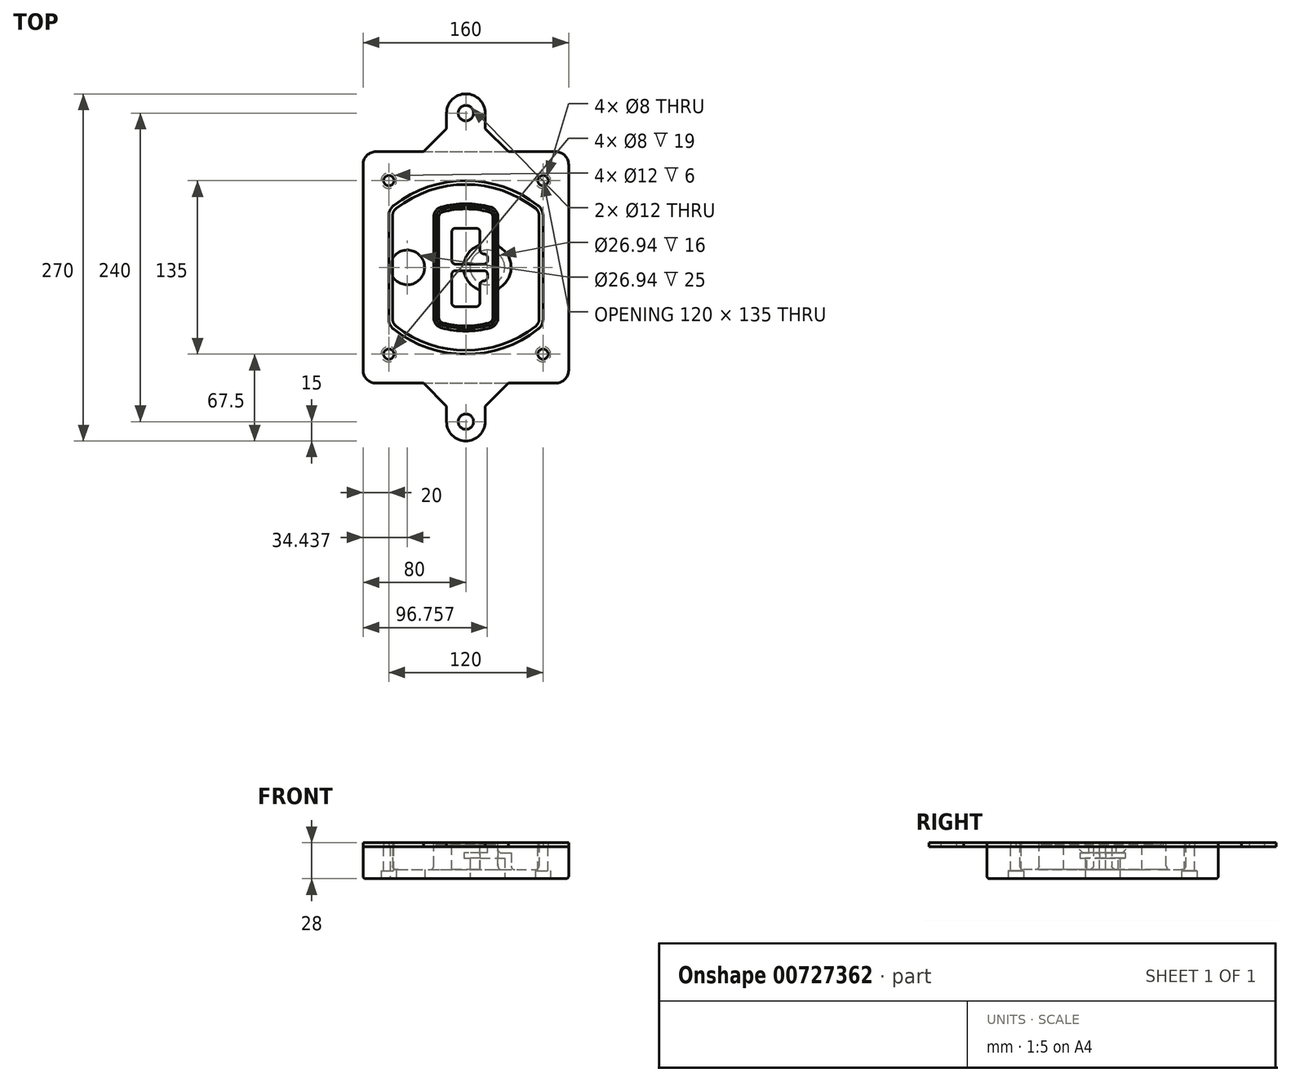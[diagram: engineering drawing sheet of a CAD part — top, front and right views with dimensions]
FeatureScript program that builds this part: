
annotation { "Feature Type Name" : "Feature", "Feature Type Description" : "" }
export const myFeature = defineFeature(function(context is Context, id is Id, definition is map)
    precondition{}
    {
        {
            var Q0;
            Q0=qCreatedBy(makeId("Top.planeOp"),FACE);
            var sketch = newSketch(context, id + "F0", { "sketchPlane" : qUnion([Q0])});
            skPoint(sketch, "E0.rect.middle", {"position": v(0, 0) * mm});
            skLineSegment(sketch, "E1.bottom", {"start": v(-70, -90) * mm, "end": v(70, -90) * mm});
            skLineSegment(sketch, "E1.top", {"start": v(-70, 90) * mm, "end": v(70, 90) * mm});
            skLineSegment(sketch, "E1.left", {"start": v(-80, -80) * mm, "end": v(-80, 80) * mm});
            skLineSegment(sketch, "E1.right", {"start": v(80, -80) * mm, "end": v(80, 80) * mm});
            skLineSegment(sketch, "E2", {"start": v(-80, 90) * mm, "end": v(80, -90) * mm, "construction": true});
            skLineSegment(sketch, "E3", {"start": v(80, 90) * mm, "end": v(-80, -90) * mm, "construction": true});
            skCircle(sketch, "E4", {"center": v(-60, 67.5) * mm, "radius": 4 * mm});
            skCircle(sketch, "E5", {"center": v(60, 67.5) * mm, "radius": 4 * mm});
            skCircle(sketch, "E6", {"center": v(60, -67.5) * mm, "radius": 4 * mm});
            skCircle(sketch, "E7", {"center": v(-60, -67.5) * mm, "radius": 4 * mm});
            skLineSegment(sketch, "E8", {"start": v(-60, 67.5) * mm, "end": v(60, 67.5) * mm, "construction": true});
            skLineSegment(sketch, "E9", {"start": v(60, 67.5) * mm, "end": v(60, -67.5) * mm, "construction": true});
            skLineSegment(sketch, "E10", {"start": v(60, -67.5) * mm, "end": v(-60, -67.5) * mm, "construction": true});
            skLineSegment(sketch, "E11", {"start": v(-60, -67.5) * mm, "end": v(-60, 67.5) * mm, "construction": true});
            skLineSegment(sketch, "E12", {"start": v(-60, 40.3) * mm, "end": v(-60, -40.3) * mm});
            skLineSegment(sketch, "E13", {"start": v(60, 40.3) * mm, "end": v(60, -40.3) * mm});
            skArc(sketch, "E14", {"start": v(56.15, 48.18) * mm, "mid": v(0, 67.5) * mm, "end": v(-56.15, 48.18) * mm});
            skArc(sketch, "E15", {"start": v(-56.15, -48.18) * mm, "mid": v(0, -67.5) * mm, "end": v(56.15, -48.18) * mm});
            skLineSegment(sketch, "E16", {"start": v(-60, 0) * mm, "end": v(60, 0) * mm, "construction": true});
            skPoint(sketch, "E17.visualSharp", {"position": v(-60, -45) * mm});
            skArc(sketch, "E17.filletArc", {"start": v(-60, -40.3) * mm, "mid": v(-58.99, -44.68) * mm, "end": v(-56.15, -48.18) * mm});
            skPoint(sketch, "E18.visualSharp", {"position": v(-60, 45) * mm});
            skArc(sketch, "E18.filletArc", {"start": v(-56.15, 48.18) * mm, "mid": v(-58.99, 44.68) * mm, "end": v(-60, 40.3) * mm});
            skPoint(sketch, "E19.visualSharp", {"position": v(60, 45) * mm});
            skArc(sketch, "E19.filletArc", {"start": v(60, 40.3) * mm, "mid": v(58.99, 44.68) * mm, "end": v(56.15, 48.18) * mm});
            skPoint(sketch, "E20.visualSharp", {"position": v(60, -45) * mm});
            skArc(sketch, "E20.filletArc", {"start": v(56.15, -48.18) * mm, "mid": v(58.99, -44.68) * mm, "end": v(60, -40.3) * mm});
            skPoint(sketch, "E21.visualSharp", {"position": v(-80, 90) * mm});
            skArc(sketch, "E21.filletArc", {"start": v(-70, 90) * mm, "mid": v(-77.07, 87.07) * mm, "end": v(-80, 80) * mm});
            skPoint(sketch, "E22.visualSharp", {"position": v(80, 90) * mm});
            skArc(sketch, "E22.filletArc", {"start": v(80, 80) * mm, "mid": v(77.07, 87.07) * mm, "end": v(70, 90) * mm});
            skPoint(sketch, "E23.visualSharp", {"position": v(80, -90) * mm});
            skArc(sketch, "E23.filletArc", {"start": v(70, -90) * mm, "mid": v(77.07, -87.07) * mm, "end": v(80, -80) * mm});
            skPoint(sketch, "E24.visualSharp", {"position": v(-80, -90) * mm});
            skArc(sketch, "E24.filletArc", {"start": v(-80, -80) * mm, "mid": v(-77.07, -87.07) * mm, "end": v(-70, -90) * mm});
            skArc(sketch, "E25.0", {"start": v(57, 40.3) * mm, "mid": v(56.3, 43.36) * mm, "end": v(54.3, 45.81) * mm});
            skLineSegment(sketch, "E25.1", {"start": v(57, 40.3) * mm, "end": v(57, -40.3) * mm});
            skArc(sketch, "E25.2", {"start": v(54.3, -45.81) * mm, "mid": v(56.3, -43.36) * mm, "end": v(57, -40.3) * mm});
            skArc(sketch, "E25.3", {"start": v(-54.3, -45.81) * mm, "mid": v(0, -64.5) * mm, "end": v(54.3, -45.81) * mm});
            skArc(sketch, "E25.4", {"start": v(-57, -40.3) * mm, "mid": v(-56.3, -43.36) * mm, "end": v(-54.3, -45.81) * mm});
            skArc(sketch, "E25.5", {"start": v(54.3, 45.81) * mm, "mid": v(0, 64.5) * mm, "end": v(-54.3, 45.81) * mm});
            skLineSegment(sketch, "E25.6", {"start": v(-57, 40.3) * mm, "end": v(-57, -40.3) * mm});
            skArc(sketch, "E25.7", {"start": v(-54.3, 45.81) * mm, "mid": v(-56.3, 43.36) * mm, "end": v(-57, 40.3) * mm});
            skArc(sketch, "E26.0", {"start": v(-58.62, 51.33) * mm, "mid": v(-62.58, 46.43) * mm, "end": v(-64, 40.3) * mm});
            skArc(sketch, "E26.1", {"start": v(58.62, 51.33) * mm, "mid": v(0, 71.5) * mm, "end": v(-58.62, 51.33) * mm});
            skArc(sketch, "E26.2", {"start": v(64, 40.3) * mm, "mid": v(62.58, 46.43) * mm, "end": v(58.62, 51.33) * mm});
            skLineSegment(sketch, "E26.3", {"start": v(64, 40.3) * mm, "end": v(64, -40.3) * mm});
            skArc(sketch, "E26.4", {"start": v(58.62, -51.33) * mm, "mid": v(62.58, -46.43) * mm, "end": v(64, -40.3) * mm});
            skLineSegment(sketch, "E26.5", {"start": v(-64, 40.3) * mm, "end": v(-64, -40.3) * mm});
            skArc(sketch, "E26.6", {"start": v(-58.62, -51.33) * mm, "mid": v(0, -71.5) * mm, "end": v(58.62, -51.33) * mm});
            skArc(sketch, "E26.7", {"start": v(-64, -40.3) * mm, "mid": v(-62.58, -46.43) * mm, "end": v(-58.62, -51.33) * mm});
            skSolve(sketch);
        }
        {
            var Q0;
            Q0=makeQuery(id+"F0.imprint","IMPRINT",FACE,{"disambiguationData":[TD([[makeQuery(id+"F0.imprint","IMPRINT",EDGE,{"derivedFrom":sQuery(id+"F0.wireOp",EDGE,"E1.bottom")}),1.0]])]});
            var Q1;
            Q1=makeQuery(id+"F0.imprint","IMPRINT",FACE,{"disambiguationData":[TD([[makeQuery(id+"F0.imprint","IMPRINT",EDGE,{"derivedFrom":sQuery(id+"F0.wireOp",EDGE,"E12")}),1.0]])]});
            var Q2;
            Q2=makeQuery(id+"F0.imprint","IMPRINT",FACE,{"disambiguationData":[TD([[makeQuery(id+"F0.imprint","IMPRINT",EDGE,{"derivedFrom":sQuery(id+"F0.wireOp",EDGE,"E25.0")}),1.0]])]});
            var Q3;
            Q3=makeQuery(id+"F0.imprint","IMPRINT",FACE,{"disambiguationData":[TD([[makeQuery(id+"F0.imprint","IMPRINT",EDGE,{"derivedFrom":sQuery(id+"F0.wireOp",EDGE,"E12")}),-1.0]])]});
            extrude(context, id + "F1", {"entities" : qUnion([Q0, Q1, Q2, Q3]), "oppositeDirection" : true, "depth" : 25 * mm});
        }
        {
            var Q0;
            Q0=makeQuery(id+"F0.imprint","IMPRINT",FACE,{"disambiguationData":[TD([[makeQuery(id+"F0.imprint","IMPRINT",EDGE,{"derivedFrom":sQuery(id+"F0.wireOp",EDGE,"E12")}),1.0]])]});
            extrude(context, id + "F2", {"entities" : qUnion([Q0]), "operationType" : NewBodyOperationType.ADD, "depth" : 3 * mm});
        }
        {
            var Q0;
            Q0=makeQuery(id+"F0.imprint","IMPRINT",FACE,{"disambiguationData":[TD([[makeQuery(id+"F0.imprint","IMPRINT",EDGE,{"derivedFrom":sQuery(id+"F0.wireOp",EDGE,"E25.0")}),1.0]])]});
            extrude(context, id + "F3", {"entities" : qUnion([Q0]), "operationType" : NewBodyOperationType.REMOVE, "oppositeDirection" : true, "depth" : 18 * mm});
        }
        {
            var Q0;
            Q0=makeQuery(id+"F2.opExtrude","CAP_FACE",FACE,{"disambiguationData":[OSD([sQuery(id+"F0.wireOp",EDGE,"E12"),sQuery(id+"F0.wireOp",EDGE,"E13"),sQuery(id+"F0.wireOp",EDGE,"E14"),sQuery(id+"F0.wireOp",EDGE,"E15"),sQuery(id+"F0.wireOp",EDGE,"E17.filletArc"),sQuery(id+"F0.wireOp",EDGE,"E18.filletArc"),sQuery(id+"F0.wireOp",EDGE,"E19.filletArc"),sQuery(id+"F0.wireOp",EDGE,"E20.filletArc"),sQuery(id+"F0.wireOp",EDGE,"E25.0"),sQuery(id+"F0.wireOp",EDGE,"E25.1"),sQuery(id+"F0.wireOp",EDGE,"E25.2"),sQuery(id+"F0.wireOp",EDGE,"E25.3"),sQuery(id+"F0.wireOp",EDGE,"E25.4"),sQuery(id+"F0.wireOp",EDGE,"E25.5"),sQuery(id+"F0.wireOp",EDGE,"E25.6"),sQuery(id+"F0.wireOp",EDGE,"E25.7")])],"isStart":false});
            var sketch = newSketch(context, id + "F4", { "sketchPlane" : qUnion([Q0])});
            skArc(sketch, "E27.0", {"start": v(-19.08, -46.97) * mm, "mid": v(0, -49.5) * mm, "end": v(19.08, -46.97) * mm});
            skArc(sketch, "E28.0", {"start": v(19.08, 46.97) * mm, "mid": v(0, 49.5) * mm, "end": v(-19.08, 46.97) * mm});
            skLineSegment(sketch, "E29", {"start": v(-25, 39.25) * mm, "end": v(-25, -39.25) * mm});
            skLineSegment(sketch, "E30", {"start": v(25, 39.25) * mm, "end": v(25, -39.25) * mm});
            skLineSegment(sketch, "E31", {"start": v(-25, 45.1) * mm, "end": v(25, 45.1) * mm, "construction": true});
            skLineSegment(sketch, "E32", {"start": v(-25, -45.1) * mm, "end": v(25, -45.1) * mm, "construction": true});
            skPoint(sketch, "E33.visualSharp", {"position": v(-25, 45.1) * mm});
            skArc(sketch, "E33.filletArc", {"start": v(-19.08, 46.97) * mm, "mid": v(-23.35, 44.11) * mm, "end": v(-25, 39.25) * mm});
            skPoint(sketch, "E34.visualSharp", {"position": v(25, 45.1) * mm});
            skArc(sketch, "E34.filletArc", {"start": v(25, 39.25) * mm, "mid": v(23.35, 44.11) * mm, "end": v(19.08, 46.97) * mm});
            skPoint(sketch, "E35.visualSharp", {"position": v(25, -45.1) * mm});
            skArc(sketch, "E35.filletArc", {"start": v(19.08, -46.97) * mm, "mid": v(23.35, -44.11) * mm, "end": v(25, -39.25) * mm});
            skPoint(sketch, "E36.visualSharp", {"position": v(-25, -45.1) * mm});
            skArc(sketch, "E36.filletArc", {"start": v(-25, -39.25) * mm, "mid": v(-23.35, -44.11) * mm, "end": v(-19.08, -46.97) * mm});
            skArc(sketch, "E37.0", {"start": v(54.3, 45.81) * mm, "mid": v(0, 64.5) * mm, "end": v(-54.3, 45.81) * mm});
            skArc(sketch, "E37.1", {"start": v(-54.3, 45.81) * mm, "mid": v(-56.3, 43.36) * mm, "end": v(-57, 40.3) * mm});
            skLineSegment(sketch, "E37.2", {"start": v(-57, 40.3) * mm, "end": v(-57, -40.3) * mm});
            skArc(sketch, "E37.3", {"start": v(-57, -40.3) * mm, "mid": v(-56.3, -43.36) * mm, "end": v(-54.3, -45.81) * mm});
            skArc(sketch, "E37.4", {"start": v(-54.3, -45.81) * mm, "mid": v(0, -64.5) * mm, "end": v(54.3, -45.81) * mm});
            skArc(sketch, "E37.5", {"start": v(54.3, -45.81) * mm, "mid": v(56.3, -43.36) * mm, "end": v(57, -40.3) * mm});
            skLineSegment(sketch, "E37.6", {"start": v(57, 40.3) * mm, "end": v(57, -40.3) * mm});
            skArc(sketch, "E37.7", {"start": v(57, 40.3) * mm, "mid": v(56.3, 43.36) * mm, "end": v(54.3, 45.81) * mm});
            skLineSegment(sketch, "E38.0", {"start": v(23, 39.25) * mm, "end": v(23, -39.25) * mm});
            skArc(sketch, "E38.1", {"start": v(18.56, -45.04) * mm, "mid": v(21.76, -42.9) * mm, "end": v(23, -39.25) * mm});
            skArc(sketch, "E38.2", {"start": v(-18.56, -45.04) * mm, "mid": v(0, -47.5) * mm, "end": v(18.56, -45.04) * mm});
            skArc(sketch, "E38.3", {"start": v(-23, -39.25) * mm, "mid": v(-21.76, -42.9) * mm, "end": v(-18.56, -45.04) * mm});
            skLineSegment(sketch, "E38.4", {"start": v(-23, 39.25) * mm, "end": v(-23, -39.25) * mm});
            skArc(sketch, "E38.5", {"start": v(23, 39.25) * mm, "mid": v(21.76, 42.9) * mm, "end": v(18.56, 45.04) * mm});
            skArc(sketch, "E38.6", {"start": v(-18.56, 45.04) * mm, "mid": v(-21.76, 42.9) * mm, "end": v(-23, 39.25) * mm});
            skArc(sketch, "E38.7", {"start": v(18.56, 45.04) * mm, "mid": v(0, 47.5) * mm, "end": v(-18.56, 45.04) * mm});
            skArc(sketch, "E39.0", {"start": v(21, 39.25) * mm, "mid": v(20.18, 41.68) * mm, "end": v(18.04, 43.1) * mm});
            skLineSegment(sketch, "E39.1", {"start": v(21, 39.25) * mm, "end": v(21, -39.25) * mm});
            skArc(sketch, "E39.2", {"start": v(18.04, -43.1) * mm, "mid": v(20.18, -41.68) * mm, "end": v(21, -39.25) * mm});
            skArc(sketch, "E39.3", {"start": v(-18.04, -43.1) * mm, "mid": v(0, -45.5) * mm, "end": v(18.04, -43.1) * mm});
            skArc(sketch, "E39.4", {"start": v(-21, -39.25) * mm, "mid": v(-20.18, -41.68) * mm, "end": v(-18.04, -43.1) * mm});
            skArc(sketch, "E39.5", {"start": v(18.04, 43.1) * mm, "mid": v(0, 45.5) * mm, "end": v(-18.04, 43.1) * mm});
            skLineSegment(sketch, "E39.6", {"start": v(-21, 39.25) * mm, "end": v(-21, -39.25) * mm});
            skArc(sketch, "E39.7", {"start": v(-18.04, 43.1) * mm, "mid": v(-20.18, 41.68) * mm, "end": v(-21, 39.25) * mm});
            skLineSegment(sketch, "E40", {"start": v(-25, 0) * mm, "end": v(25, 0) * mm, "construction": true});
            skLineSegment(sketch, "E41", {"start": v(-11, 5.5) * mm, "end": v(-11, 27.5) * mm});
            skLineSegment(sketch, "E42", {"start": v(-8, 30.5) * mm, "end": v(8, 30.5) * mm});
            skLineSegment(sketch, "E43", {"start": v(11, 27.5) * mm, "end": v(11, 13.5) * mm});
            skLineSegment(sketch, "E44", {"start": v(14, 10.5) * mm, "end": v(14, 10.5) * mm});
            skLineSegment(sketch, "E45", {"start": v(17, 7.5) * mm, "end": v(17, 5.5) * mm});
            skLineSegment(sketch, "E46", {"start": v(14, 2.5) * mm, "end": v(-8, 2.5) * mm});
            skPoint(sketch, "E47.visualSharp", {"position": v(-11, 30.5) * mm});
            skArc(sketch, "E47.filletArc", {"start": v(-8, 30.5) * mm, "mid": v(-10.12, 29.62) * mm, "end": v(-11, 27.5) * mm});
            skPoint(sketch, "E48.visualSharp", {"position": v(11, 30.5) * mm});
            skArc(sketch, "E48.filletArc", {"start": v(11, 27.5) * mm, "mid": v(10.12, 29.62) * mm, "end": v(8, 30.5) * mm});
            skPoint(sketch, "E49.visualSharp", {"position": v(11, 10.5) * mm});
            skArc(sketch, "E49.filletArc", {"start": v(11, 13.5) * mm, "mid": v(11.88, 11.38) * mm, "end": v(14, 10.5) * mm});
            skPoint(sketch, "E50.visualSharp", {"position": v(17, 10.5) * mm});
            skArc(sketch, "E50.filletArc", {"start": v(17, 7.5) * mm, "mid": v(16.12, 9.62) * mm, "end": v(14, 10.5) * mm});
            skPoint(sketch, "E51.visualSharp", {"position": v(17, 2.5) * mm});
            skArc(sketch, "E51.filletArc", {"start": v(14, 2.5) * mm, "mid": v(16.12, 3.38) * mm, "end": v(17, 5.5) * mm});
            skPoint(sketch, "E52.visualSharp", {"position": v(-11, 2.5) * mm});
            skArc(sketch, "E52.filletArc", {"start": v(-11, 5.5) * mm, "mid": v(-10.12, 3.38) * mm, "end": v(-8, 2.5) * mm});
            skLineSegment(sketch, "E53.0.MirrorCS", {"start": v(14, -2.5) * mm, "end": v(-8, -2.5) * mm});
            skArc(sketch, "E54.0.MirrorCS", {"start": v(-11, -5.5) * mm, "mid": v(-10.12, -3.38) * mm, "end": v(-8, -2.5) * mm});
            skLineSegment(sketch, "E55.0.MirrorCS", {"start": v(-11, -5.5) * mm, "end": v(-11, -27.5) * mm});
            skArc(sketch, "E56.0.MirrorCS", {"start": v(-8, -30.5) * mm, "mid": v(-10.12, -29.62) * mm, "end": v(-11, -27.5) * mm});
            skLineSegment(sketch, "E57.0.MirrorCS", {"start": v(-8, -30.5) * mm, "end": v(8, -30.5) * mm});
            skArc(sketch, "E58.0.MirrorCS", {"start": v(11, -27.5) * mm, "mid": v(10.12, -29.62) * mm, "end": v(8, -30.5) * mm});
            skLineSegment(sketch, "E59.0.MirrorCS", {"start": v(11, -27.5) * mm, "end": v(11, -13.5) * mm});
            skArc(sketch, "E60.0.MirrorCS", {"start": v(11, -13.5) * mm, "mid": v(11.88, -11.38) * mm, "end": v(14, -10.5) * mm});
            skArc(sketch, "E61.0.MirrorCS", {"start": v(17, -7.5) * mm, "mid": v(16.12, -9.62) * mm, "end": v(14, -10.5) * mm});
            skLineSegment(sketch, "E62.0.MirrorCS", {"start": v(17, -7.5) * mm, "end": v(17, -5.5) * mm});
            skArc(sketch, "E63.0.MirrorCS", {"start": v(14, -2.5) * mm, "mid": v(16.12, -3.38) * mm, "end": v(17, -5.5) * mm});
            skSolve(sketch);
        }
        {
            var Q0;
            Q0=makeQuery(id+"F4.imprint","IMPRINT",FACE,{"disambiguationData":[TD([[makeQuery(id+"F4.imprint","IMPRINT",EDGE,{"derivedFrom":sQuery(id+"F4.wireOp",EDGE,"E27.0")}),1.0]])]});
            var Q1;
            Q1=makeQuery(id+"F4.imprint","IMPRINT",FACE,{"disambiguationData":[TD([[makeQuery(id+"F4.imprint","IMPRINT",EDGE,{"derivedFrom":sQuery(id+"F4.wireOp",EDGE,"E38.0")}),-1.0]])]});
            var Q2;
            Q2=makeQuery(id+"F4.imprint","IMPRINT",FACE,{"disambiguationData":[TD([[makeQuery(id+"F4.imprint","IMPRINT",EDGE,{"derivedFrom":sQuery(id+"F4.wireOp",EDGE,"E39.0")}),1.0]])]});
            extrude(context, id + "F5", {"entities" : qUnion([Q0, Q1, Q2]), "operationType" : NewBodyOperationType.ADD, "endBound" : BoundingType.UP_TO_NEXT, "oppositeDirection" : true, "depth" : 25 * mm});
        }
        {
            var Q0;
            Q0=makeQuery(id+"F4.imprint","IMPRINT",FACE,{"disambiguationData":[TD([[makeQuery(id+"F4.imprint","IMPRINT",EDGE,{"derivedFrom":sQuery(id+"F4.wireOp",EDGE,"E38.0")}),-1.0]])]});
            extrude(context, id + "F6", {"entities" : qUnion([Q0]), "operationType" : NewBodyOperationType.REMOVE, "oppositeDirection" : true, "depth" : 2 * mm});
        }
        {
            var Q0;
            Q0=makeQuery(id+"F1.opExtrude","CAP_FACE",FACE,{"disambiguationData":[OSD([sQuery(id+"F0.wireOp",EDGE,"E1.bottom"),sQuery(id+"F0.wireOp",EDGE,"E1.top"),sQuery(id+"F0.wireOp",EDGE,"E1.left"),sQuery(id+"F0.wireOp",EDGE,"E1.right"),sQuery(id+"F0.wireOp",EDGE,"E4"),sQuery(id+"F0.wireOp",EDGE,"E5"),sQuery(id+"F0.wireOp",EDGE,"E6"),sQuery(id+"F0.wireOp",EDGE,"E7"),sQuery(id+"F0.wireOp",EDGE,"E21.filletArc"),sQuery(id+"F0.wireOp",EDGE,"E22.filletArc"),sQuery(id+"F0.wireOp",EDGE,"E23.filletArc"),sQuery(id+"F0.wireOp",EDGE,"E24.filletArc")])],"isStart":false});
            var sketch = newSketch(context, id + "F7", { "sketchPlane" : qUnion([Q0])});
            skCircle(sketch, "E64", {"center": v(16.76, 0) * mm, "radius": 13.47 * mm});
            skCircle(sketch, "E65", {"center": v(-45.56, 0) * mm, "radius": 13.47 * mm});
            skLineSegment(sketch, "E66", {"start": v(80, 0) * mm, "end": v(-80, 0) * mm});
            skCircle(sketch, "E67", {"center": v(16.76, 0) * mm, "radius": 18.47 * mm});
            skCircle(sketch, "E68", {"center": v(60, -67.5) * mm, "radius": 6 * mm});
            skCircle(sketch, "E69", {"center": v(-60, -67.5) * mm, "radius": 6 * mm});
            skCircle(sketch, "E70", {"center": v(-60, 67.5) * mm, "radius": 6 * mm});
            skCircle(sketch, "E71", {"center": v(60, 67.5) * mm, "radius": 6 * mm});
            skSolve(sketch);
        }
        {
            var Q0;
            {var subQ1=sQuery(id+"F7.wireOp",EDGE,"E66");var subQ4=sQuery(id+"F7.wireOp",EDGE,"E64");var subQ6=makeQuery(id+"F7.imprint","INTERSECT",VERTEX,{"disambiguationData":[OD(0.0)],"derivedFrom":[subQ4,subQ1]});Q0=makeQuery(id+"F7.imprint","IMPRINT",FACE,{"disambiguationData":[TD([[makeQuery(id+"F7.imprint","IMPRINT",EDGE,{"disambiguationData":[TD([[subQ6,-1.0]])],"derivedFrom":subQ4}),-1.0]])]});}
            var Q1;
            {var subQ0=sQuery(id+"F7.wireOp",EDGE,"E66");var subQ1=sQuery(id+"F7.wireOp",EDGE,"E64");var subQ3=makeQuery(id+"F7.imprint","INTERSECT",VERTEX,{"disambiguationData":[OD(0.0)],"derivedFrom":[subQ1,subQ0]});Q1=makeQuery(id+"F7.imprint","IMPRINT",FACE,{"disambiguationData":[TD([[makeQuery(id+"F7.imprint","IMPRINT",EDGE,{"disambiguationData":[TD([[subQ3,-1.0]])],"derivedFrom":subQ1}),1.0]])]});}
            var Q2;
            {var subQ0=sQuery(id+"F7.wireOp",EDGE,"E66");var subQ1=sQuery(id+"F7.wireOp",EDGE,"E64");var subQ3=makeQuery(id+"F7.imprint","INTERSECT",VERTEX,{"disambiguationData":[OD(0.0)],"derivedFrom":[subQ1,subQ0]});Q2=makeQuery(id+"F7.imprint","IMPRINT",FACE,{"disambiguationData":[TD([[makeQuery(id+"F7.imprint","IMPRINT",EDGE,{"disambiguationData":[TD([[subQ3,1.0]])],"derivedFrom":subQ1}),1.0]])]});}
            var Q3;
            {var subQ1=sQuery(id+"F7.wireOp",EDGE,"E66");var subQ4=sQuery(id+"F7.wireOp",EDGE,"E64");var subQ6=makeQuery(id+"F7.imprint","INTERSECT",VERTEX,{"disambiguationData":[OD(0.0)],"derivedFrom":[subQ4,subQ1]});Q3=makeQuery(id+"F7.imprint","IMPRINT",FACE,{"disambiguationData":[TD([[makeQuery(id+"F7.imprint","IMPRINT",EDGE,{"disambiguationData":[TD([[subQ6,1.0]])],"derivedFrom":subQ4}),-1.0]])]});}
            extrude(context, id + "F8", {"entities" : qUnion([Q0, Q1, Q2, Q3]), "operationType" : NewBodyOperationType.ADD, "oppositeDirection" : true, "depth" : 20 * mm});
        }
        {
            var Q0;
            {var subQ0=sQuery(id+"F7.wireOp",EDGE,"E66");var subQ1=sQuery(id+"F7.wireOp",EDGE,"E64");var subQ3=makeQuery(id+"F7.imprint","INTERSECT",VERTEX,{"disambiguationData":[OD(0.0)],"derivedFrom":[subQ1,subQ0]});Q0=makeQuery(id+"F7.imprint","IMPRINT",FACE,{"disambiguationData":[TD([[makeQuery(id+"F7.imprint","IMPRINT",EDGE,{"disambiguationData":[TD([[subQ3,-1.0]])],"derivedFrom":subQ1}),1.0]])]});}
            var Q1;
            {var subQ0=sQuery(id+"F7.wireOp",EDGE,"E66");var subQ1=sQuery(id+"F7.wireOp",EDGE,"E64");var subQ3=makeQuery(id+"F7.imprint","INTERSECT",VERTEX,{"disambiguationData":[OD(0.0)],"derivedFrom":[subQ1,subQ0]});Q1=makeQuery(id+"F7.imprint","IMPRINT",FACE,{"disambiguationData":[TD([[makeQuery(id+"F7.imprint","IMPRINT",EDGE,{"disambiguationData":[TD([[subQ3,1.0]])],"derivedFrom":subQ1}),1.0]])]});}
            extrude(context, id + "F9", {"entities" : qUnion([Q0, Q1]), "operationType" : NewBodyOperationType.REMOVE, "oppositeDirection" : true, "depth" : 16 * mm});
        }
        {
            var Q0;
            {var subQ0=sQuery(id+"F7.wireOp",EDGE,"E66");var subQ1=sQuery(id+"F7.wireOp",EDGE,"E65");var subQ3=makeQuery(id+"F7.imprint","INTERSECT",VERTEX,{"disambiguationData":[OD(0.0)],"derivedFrom":[subQ1,subQ0]});Q0=makeQuery(id+"F7.imprint","IMPRINT",FACE,{"disambiguationData":[TD([[makeQuery(id+"F7.imprint","IMPRINT",EDGE,{"disambiguationData":[TD([[subQ3,-1.0]])],"derivedFrom":subQ1}),1.0]])]});}
            var Q1;
            {var subQ0=sQuery(id+"F7.wireOp",EDGE,"E66");var subQ1=sQuery(id+"F7.wireOp",EDGE,"E65");var subQ3=makeQuery(id+"F7.imprint","INTERSECT",VERTEX,{"disambiguationData":[OD(0.0)],"derivedFrom":[subQ1,subQ0]});Q1=makeQuery(id+"F7.imprint","IMPRINT",FACE,{"disambiguationData":[TD([[makeQuery(id+"F7.imprint","IMPRINT",EDGE,{"disambiguationData":[TD([[subQ3,1.0]])],"derivedFrom":subQ1}),1.0]])]});}
            extrude(context, id + "F10", {"entities" : qUnion([Q0, Q1]), "operationType" : NewBodyOperationType.REMOVE, "oppositeDirection" : true, "depth" : 25 * mm});
        }
        {
            var Q0;
            Q0=makeQuery(id+"F7.imprint","IMPRINT",FACE,{"disambiguationData":[TD([[makeQuery(id+"F7.imprint","IMPRINT",EDGE,{"derivedFrom":sQuery(id+"F7.wireOp",EDGE,"E68")}),1.0]])]});
            var Q1;
            Q1=makeQuery(id+"F7.imprint","IMPRINT",FACE,{"disambiguationData":[TD([[makeQuery(id+"F7.imprint","IMPRINT",EDGE,{"derivedFrom":makeQuery(id+"F1.opExtrude","CAP_EDGE",EDGE,{"disambiguationData":[OSD([sQuery(id+"F0.wireOp",EDGE,"E5")])],"isStart":false})}),-1.0]])]});
            var Q2;
            Q2=makeQuery(id+"F7.imprint","IMPRINT",FACE,{"disambiguationData":[TD([[makeQuery(id+"F7.imprint","IMPRINT",EDGE,{"derivedFrom":sQuery(id+"F7.wireOp",EDGE,"E69")}),1.0]])]});
            var Q3;
            Q3=makeQuery(id+"F7.imprint","IMPRINT",FACE,{"disambiguationData":[TD([[makeQuery(id+"F7.imprint","IMPRINT",EDGE,{"derivedFrom":makeQuery(id+"F1.opExtrude","CAP_EDGE",EDGE,{"disambiguationData":[OSD([sQuery(id+"F0.wireOp",EDGE,"E4")])],"isStart":false})}),-1.0]])]});
            var Q4;
            Q4=makeQuery(id+"F7.imprint","IMPRINT",FACE,{"disambiguationData":[TD([[makeQuery(id+"F7.imprint","IMPRINT",EDGE,{"derivedFrom":sQuery(id+"F7.wireOp",EDGE,"E70")}),1.0]])]});
            var Q5;
            Q5=makeQuery(id+"F7.imprint","IMPRINT",FACE,{"disambiguationData":[TD([[makeQuery(id+"F7.imprint","IMPRINT",EDGE,{"derivedFrom":makeQuery(id+"F1.opExtrude","CAP_EDGE",EDGE,{"disambiguationData":[OSD([sQuery(id+"F0.wireOp",EDGE,"E7")])],"isStart":false})}),-1.0]])]});
            var Q6;
            Q6=makeQuery(id+"F7.imprint","IMPRINT",FACE,{"disambiguationData":[TD([[makeQuery(id+"F7.imprint","IMPRINT",EDGE,{"derivedFrom":sQuery(id+"F7.wireOp",EDGE,"E71")}),1.0]])]});
            var Q7;
            Q7=makeQuery(id+"F7.imprint","IMPRINT",FACE,{"disambiguationData":[TD([[makeQuery(id+"F7.imprint","IMPRINT",EDGE,{"derivedFrom":makeQuery(id+"F1.opExtrude","CAP_EDGE",EDGE,{"disambiguationData":[OSD([sQuery(id+"F0.wireOp",EDGE,"E6")])],"isStart":false})}),-1.0]])]});
            extrude(context, id + "F11", {"entities" : qUnion([Q0, Q1, Q2, Q3, Q4, Q5, Q6, Q7]), "operationType" : NewBodyOperationType.REMOVE, "oppositeDirection" : true, "depth" : 6 * mm});
        }
        {
            var Q0;
            Q0=makeQuery(id+"F9.boolean.opBoolean","COPY",FACE,{"derivedFrom":makeQuery(id+"F9.opExtrude","CAP_FACE",FACE,{"disambiguationData":[OSD([sQuery(id+"F7.wireOp",EDGE,"E64")])],"isStart":false})});
            var sketch = newSketch(context, id + "F12", { "sketchPlane" : qUnion([Q0])});
            skArc(sketch, "E72.0", {"start": v(11, 17.55) * mm, "mid": v(2.57, 11.82) * mm, "end": v(-1.54, 2.5) * mm});
            skArc(sketch, "E72.1", {"start": v(-1.54, -2.5) * mm, "mid": v(2.57, -11.82) * mm, "end": v(11, -17.55) * mm});
            skLineSegment(sketch, "E73", {"start": v(-1.54, -2.5) * mm, "end": v(14, -2.5) * mm});
            skLineSegment(sketch, "E74.0", {"start": v(14, 2.5) * mm, "end": v(-1.54, 2.5) * mm});
            skArc(sketch, "E74.1", {"start": v(14, 2.5) * mm, "mid": v(16.12, 3.38) * mm, "end": v(17, 5.5) * mm});
            skLineSegment(sketch, "E74.2", {"start": v(17, 7.5) * mm, "end": v(17, 5.5) * mm});
            skArc(sketch, "E74.3", {"start": v(17, 7.5) * mm, "mid": v(16.12, 9.62) * mm, "end": v(14, 10.5) * mm});
            skArc(sketch, "E74.4", {"start": v(11, 13.5) * mm, "mid": v(11.88, 11.38) * mm, "end": v(14, 10.5) * mm});
            skLineSegment(sketch, "E74.5", {"start": v(11, 17.55) * mm, "end": v(11, 13.5) * mm});
            skLineSegment(sketch, "E74.7", {"start": v(14, -2.5) * mm, "end": v(-1.54, -2.5) * mm});
            skArc(sketch, "E74.8", {"start": v(14, -2.5) * mm, "mid": v(16.12, -3.38) * mm, "end": v(17, -5.5) * mm});
            skLineSegment(sketch, "E74.9", {"start": v(17, -7.5) * mm, "end": v(17, -5.5) * mm});
            skArc(sketch, "E74.10", {"start": v(17, -7.5) * mm, "mid": v(16.12, -9.62) * mm, "end": v(14, -10.5) * mm});
            skArc(sketch, "E74.11", {"start": v(11, -13.5) * mm, "mid": v(11.88, -11.38) * mm, "end": v(14, -10.5) * mm});
            skLineSegment(sketch, "E74.12", {"start": v(11, -17.55) * mm, "end": v(11, -13.5) * mm});
            skPoint(sketch, "E75.orphan", {"position": v(11, -27.5) * mm});
            skPoint(sketch, "E76.orphan", {"position": v(-8, -2.5) * mm});
            skPoint(sketch, "E77.orphan", {"position": v(-8, 2.5) * mm});
            skPoint(sketch, "E78.orphan", {"position": v(11, 27.5) * mm});
            skSolve(sketch);
        }
        {
            var Q0;
            {var subQ7=sQuery(id+"F12.wireOp",EDGE,"E72.0");var subQ14=sQuery(id+"F12.wireOp",EDGE,"E72.1");var subQ16=sQuery(id+"F12.wireOp",EDGE,"E74.1");var subQ18=sQuery(id+"F12.wireOp",EDGE,"E74.8");Q0=qUnion([makeQuery(id+"F12.imprint","IMPRINT",FACE,{"disambiguationData":[TD([[makeQuery(id+"F12.imprint","IMPRINT",EDGE,{"derivedFrom":subQ7}),1.0]])]}),makeQuery(id+"F12.imprint","IMPRINT",FACE,{"disambiguationData":[TD([[makeQuery(id+"F12.imprint","IMPRINT",EDGE,{"derivedFrom":subQ14}),1.0]])]}),makeQuery(id+"F12.imprint","IMPRINT",FACE,{"disambiguationData":[TD([[makeQuery(id+"F12.imprint","IMPRINT",EDGE,{"derivedFrom":subQ16}),1.0]])]}),makeQuery(id+"F12.imprint","IMPRINT",FACE,{"disambiguationData":[TD([[makeQuery(id+"F12.imprint","IMPRINT",EDGE,{"derivedFrom":subQ18}),-1.0]])]})]);}
            var Q1;
            Q1=makeQuery(id+"F5.boolean.opBoolean","SPLIT",FACE,{"disambiguationData":[TD([makeQuery(id+"F5.opExtrude","SWEPT_FACE",FACE,{"disambiguationData":[OSD([sQuery(id+"F4.wireOp",EDGE,"E41")])]})])],"derivedFrom":makeQuery(id+"F3.boolean.opBoolean","COPY",FACE,{"derivedFrom":makeQuery(id+"F3.opExtrude","CAP_FACE",FACE,{"disambiguationData":[OSD([sQuery(id+"F0.wireOp",EDGE,"E25.0"),sQuery(id+"F0.wireOp",EDGE,"E25.1"),sQuery(id+"F0.wireOp",EDGE,"E25.2"),sQuery(id+"F0.wireOp",EDGE,"E25.3"),sQuery(id+"F0.wireOp",EDGE,"E25.4"),sQuery(id+"F0.wireOp",EDGE,"E25.5"),sQuery(id+"F0.wireOp",EDGE,"E25.6"),sQuery(id+"F0.wireOp",EDGE,"E25.7")])],"isStart":false})})});
            extrude(context, id + "F13", {"entities" : qUnion([Q0]), "operationType" : NewBodyOperationType.REMOVE, "endBound" : BoundingType.UP_TO_SURFACE, "endBoundEntityFace" : qUnion([Q1]), "depth" : 25 * mm});
        }
        {
            var Q0;
            Q0=makeQuery(id+"F3.boolean.opBoolean","COPY",EDGE,{"derivedFrom":makeQuery(id+"F3.opExtrude","CAP_EDGE",EDGE,{"disambiguationData":[OSD([sQuery(id+"F0.wireOp",EDGE,"E25.6")])],"isStart":false})});
            var Q1;
            Q1=makeQuery(id+"F8.boolean.opBoolean","INTERSECT",EDGE,{"derivedFrom":[makeQuery(id+"F5.opExtrude","SWEPT_FACE",FACE,{"disambiguationData":[OSD([sQuery(id+"F4.wireOp",EDGE,"E30")])]}),makeQuery(id+"F8.opExtrude","CAP_FACE",FACE,{"disambiguationData":[OSD([sQuery(id+"F7.wireOp",EDGE,"E67")])],"isStart":false})]});
            var Q2;
            Q2=makeQuery(id+"F8.boolean.opBoolean","INTERSECT",EDGE,{"disambiguationData":[OD(1.0)],"derivedFrom":[makeQuery(id+"F5.opExtrude","SWEPT_FACE",FACE,{"disambiguationData":[OSD([sQuery(id+"F4.wireOp",EDGE,"E30")])]}),makeQuery(id+"F8.opExtrude","SWEPT_FACE",FACE,{"disambiguationData":[OSD([sQuery(id+"F7.wireOp",EDGE,"E67")])]})]});
            var Q3;
            {var subQ0=sQuery(id+"F4.wireOp",EDGE,"E30");Q3=makeQuery(id+"F8.boolean.opBoolean","SPLIT",EDGE,{"disambiguationData":[TD([makeQuery(id+"F5.opExtrude","SWEPT_FACE",FACE,{"disambiguationData":[OSD([sQuery(id+"F4.wireOp",EDGE,"E35.filletArc")])]})])],"derivedFrom":makeQuery(id+"F5.opExtrude","CAP_EDGE",EDGE,{"disambiguationData":[OSD([subQ0])],"isStart":false})});}
            var Q4;
            {var subQ0=sQuery(id+"F0.wireOp",EDGE,"E25.7");var subQ1=sQuery(id+"F0.wireOp",EDGE,"E25.1");var subQ2=sQuery(id+"F0.wireOp",EDGE,"E25.6");var subQ3=sQuery(id+"F0.wireOp",EDGE,"E25.5");var subQ4=sQuery(id+"F0.wireOp",EDGE,"E25.4");var subQ5=sQuery(id+"F0.wireOp",EDGE,"E25.0");var subQ6=sQuery(id+"F0.wireOp",EDGE,"E25.2");var subQ7=sQuery(id+"F0.wireOp",EDGE,"E25.3");Q4=makeQuery(id+"F8.boolean.opBoolean","INTERSECT",EDGE,{"derivedFrom":[makeQuery(id+"F5.boolean.opBoolean","SPLIT",FACE,{"disambiguationData":[TD([makeQuery(id+"F2.opExtrude","SWEPT_FACE",FACE,{"disambiguationData":[OSD([subQ5])]})])],"derivedFrom":makeQuery(id+"F3.boolean.opBoolean","COPY",FACE,{"derivedFrom":makeQuery(id+"F3.opExtrude","CAP_FACE",FACE,{"disambiguationData":[OSD([subQ5,subQ1,subQ6,subQ7,subQ4,subQ3,subQ2,subQ0])],"isStart":false})})}),makeQuery(id+"F8.opExtrude","SWEPT_FACE",FACE,{"disambiguationData":[OSD([sQuery(id+"F7.wireOp",EDGE,"E67")])]})]});}
            var Q5;
            Q5=makeQuery(id+"F8.boolean.opBoolean","INTERSECT",EDGE,{"disambiguationData":[OD(0.0)],"derivedFrom":[makeQuery(id+"F5.opExtrude","SWEPT_FACE",FACE,{"disambiguationData":[OSD([sQuery(id+"F4.wireOp",EDGE,"E30")])]}),makeQuery(id+"F8.opExtrude","SWEPT_FACE",FACE,{"disambiguationData":[OSD([sQuery(id+"F7.wireOp",EDGE,"E67")])]})]});
            fillet(context, id + "F14", {"entities" : qUnion([Q0, Q1, Q2, Q3, Q4, Q5]), "radius" : 3 * mm, "tangentPropagation" : true, "allowEdgeOverflow" : false});
        }
        {
            var Q0;
            Q0=makeQuery(id+"F1.opExtrude","CAP_EDGE",EDGE,{"disambiguationData":[OSD([sQuery(id+"F0.wireOp",EDGE,"E1.bottom")])],"isStart":false});
            fillet(context, id + "F15", {"entities" : qUnion([Q0]), "radius" : 2 * mm, "tangentPropagation" : true, "allowEdgeOverflow" : false});
        }
        {
            var Q0;
            {var subQ0=sQuery(id+"F0.wireOp",EDGE,"E21.filletArc");var subQ1=sQuery(id+"F0.wireOp",EDGE,"E7");var subQ2=sQuery(id+"F0.wireOp",EDGE,"E6");var subQ3=sQuery(id+"F0.wireOp",EDGE,"E5");var subQ4=sQuery(id+"F0.wireOp",EDGE,"E4");var subQ5=sQuery(id+"F0.wireOp",EDGE,"E22.filletArc");var subQ6=sQuery(id+"F0.wireOp",EDGE,"E1.bottom");var subQ7=sQuery(id+"F0.wireOp",EDGE,"E1.right");var subQ8=sQuery(id+"F0.wireOp",EDGE,"E1.top");var subQ9=sQuery(id+"F0.wireOp",EDGE,"E1.left");var subQ10=sQuery(id+"F0.wireOp",EDGE,"E23.filletArc");var subQ11=sQuery(id+"F0.wireOp",EDGE,"E24.filletArc");Q0=makeQuery(id+"F2.boolean.opBoolean","SPLIT",FACE,{"disambiguationData":[TD([makeQuery(id+"F1.opExtrude","SWEPT_FACE",FACE,{"disambiguationData":[OSD([subQ6])]})])],"derivedFrom":makeQuery(id+"F1.opExtrude","CAP_FACE",FACE,{"disambiguationData":[OSD([subQ6,subQ8,subQ9,subQ7,subQ4,subQ3,subQ2,subQ1,subQ0,subQ5,subQ10,subQ11])],"isStart":true})});}
            var sketch = newSketch(context, id + "F16", { "sketchPlane" : qUnion([Q0])});
            skLineSegment(sketch, "E79.0", {"start": v(-70, -90) * mm, "end": v(70, -90) * mm});
            skLineSegment(sketch, "E79.1", {"start": v(80, -80) * mm, "end": v(80, 80) * mm});
            skArc(sketch, "E79.2", {"start": v(70, -90) * mm, "mid": v(77.07, -87.07) * mm, "end": v(80, -80) * mm});
            skArc(sketch, "E79.3", {"start": v(-80, -80) * mm, "mid": v(-77.07, -87.07) * mm, "end": v(-70, -90) * mm});
            skLineSegment(sketch, "E79.4", {"start": v(-80, -80) * mm, "end": v(-80, 80) * mm});
            skLineSegment(sketch, "E79.5", {"start": v(-33, 90) * mm, "end": v(70, 90) * mm});
            skArc(sketch, "E79.6", {"start": v(-70, 90) * mm, "mid": v(-77.07, 87.07) * mm, "end": v(-80, 80) * mm});
            skArc(sketch, "E79.7", {"start": v(80, 80) * mm, "mid": v(77.07, 87.07) * mm, "end": v(70, 90) * mm});
            skCircle(sketch, "E79.8", {"center": v(60, 67.5) * mm, "radius": 4 * mm});
            skCircle(sketch, "E79.9", {"center": v(60, -67.5) * mm, "radius": 4 * mm});
            skCircle(sketch, "E79.10", {"center": v(-60, -67.5) * mm, "radius": 4 * mm});
            skCircle(sketch, "E79.11", {"center": v(-60, 67.5) * mm, "radius": 4 * mm});
            skArc(sketch, "E79.12", {"start": v(56.15, 48.18) * mm, "mid": v(0, 67.5) * mm, "end": v(-56.15, 48.18) * mm});
            skLineSegment(sketch, "E79.13", {"start": v(-60, 40.3) * mm, "end": v(-60, -40.3) * mm});
            skArc(sketch, "E79.14", {"start": v(-56.15, -48.18) * mm, "mid": v(0, -67.5) * mm, "end": v(56.15, -48.18) * mm});
            skLineSegment(sketch, "E79.15", {"start": v(60, 40.3) * mm, "end": v(60, -40.3) * mm});
            skArc(sketch, "E79.16", {"start": v(56.15, -48.18) * mm, "mid": v(58.99, -44.68) * mm, "end": v(60, -40.3) * mm});
            skArc(sketch, "E79.17", {"start": v(-60, -40.3) * mm, "mid": v(-58.99, -44.68) * mm, "end": v(-56.15, -48.18) * mm});
            skArc(sketch, "E79.18", {"start": v(-56.15, 48.18) * mm, "mid": v(-58.99, 44.68) * mm, "end": v(-60, 40.3) * mm});
            skArc(sketch, "E79.19", {"start": v(60, 40.3) * mm, "mid": v(58.99, 44.68) * mm, "end": v(56.15, 48.18) * mm});
            skPoint(sketch, "E80.centerSnap0", {"position": v(0, 90) * mm});
            skLineSegment(sketch, "E81", {"start": v(15, 108) * mm, "end": v(33, 90) * mm});
            skLineSegment(sketch, "E82", {"start": v(-15, 108) * mm, "end": v(-33, 90) * mm});
            skLineSegment(sketch, "E83", {"start": v(-15, 108) * mm, "end": v(-15, 120) * mm});
            skLineSegment(sketch, "E84", {"start": v(15, 108) * mm, "end": v(15, 120) * mm});
            skArc(sketch, "E85", {"start": v(15, 120) * mm, "mid": v(0, 135) * mm, "end": v(-15, 120) * mm});
            skLineSegment(sketch, "E86", {"start": v(0, 90) * mm, "end": v(0, 120) * mm, "construction": true});
            skCircle(sketch, "E87", {"center": v(0, 120) * mm, "radius": 6 * mm});
            skLineSegment(sketch, "E88", {"start": v(-80, 0) * mm, "end": v(80, 0) * mm, "construction": true});
            skLineSegment(sketch, "E89.MirrorCS", {"start": v(-15, -108) * mm, "end": v(-33, -90) * mm});
            skLineSegment(sketch, "E90.MirrorCS", {"start": v(0, -90) * mm, "end": v(0, -120) * mm, "construction": true});
            skLineSegment(sketch, "E91.MirrorCS", {"start": v(15, -108) * mm, "end": v(33, -90) * mm});
            skLineSegment(sketch, "E92.MirrorCS", {"start": v(15, -108) * mm, "end": v(15, -120) * mm});
            skLineSegment(sketch, "E93.MirrorCS", {"start": v(-15, -108) * mm, "end": v(-15, -120) * mm});
            skArc(sketch, "E94.MirrorCS", {"start": v(15, -120) * mm, "mid": v(0, -135) * mm, "end": v(-15, -120) * mm});
            skCircle(sketch, "E95.MirrorC", {"center": v(0, -120) * mm, "radius": 6 * mm});
            skSolve(sketch);
        }
        {
            var Q0;
            Q0=makeQuery(id+"F16.imprint","IMPRINT",FACE,{"disambiguationData":[TD([[makeQuery(id+"F16.imprint","IMPRINT",EDGE,{"derivedFrom":sQuery(id+"F16.wireOp",EDGE,"E79.1")}),1.0]])]});
            var Q1;
            {var subQ0=sQuery(id+"F16.wireOp",EDGE,"E89.MirrorCS");Q1=makeQuery(id+"F16.imprint","IMPRINT",FACE,{"disambiguationData":[TD([[makeQuery(id+"F16.imprint","IMPRINT",EDGE,{"derivedFrom":subQ0}),-1.0]])]});}
            var Q2;
            {var subQ1=sQuery(id+"F16.wireOp",EDGE,"E81");Q2=makeQuery(id+"F16.imprint","IMPRINT",FACE,{"disambiguationData":[TD([[makeQuery(id+"F16.imprint","IMPRINT",EDGE,{"derivedFrom":subQ1}),-1.0]])]});}
            var Q3;
            Q3=makeQuery(id+"F2.opExtrude","CAP_FACE",FACE,{"disambiguationData":[OSD([sQuery(id+"F0.wireOp",EDGE,"E12"),sQuery(id+"F0.wireOp",EDGE,"E13"),sQuery(id+"F0.wireOp",EDGE,"E14"),sQuery(id+"F0.wireOp",EDGE,"E15"),sQuery(id+"F0.wireOp",EDGE,"E17.filletArc"),sQuery(id+"F0.wireOp",EDGE,"E18.filletArc"),sQuery(id+"F0.wireOp",EDGE,"E19.filletArc"),sQuery(id+"F0.wireOp",EDGE,"E20.filletArc"),sQuery(id+"F0.wireOp",EDGE,"E25.0"),sQuery(id+"F0.wireOp",EDGE,"E25.1"),sQuery(id+"F0.wireOp",EDGE,"E25.2"),sQuery(id+"F0.wireOp",EDGE,"E25.3"),sQuery(id+"F0.wireOp",EDGE,"E25.4"),sQuery(id+"F0.wireOp",EDGE,"E25.5"),sQuery(id+"F0.wireOp",EDGE,"E25.6"),sQuery(id+"F0.wireOp",EDGE,"E25.7")])],"isStart":false});
            extrude(context, id + "F17", {"entities" : qUnion([Q0, Q1, Q2]), "endBound" : BoundingType.UP_TO_SURFACE, "depth" : 25 * mm, "endBoundEntityFace" : qUnion([Q3]), "offsetDistance" : 25 * mm});
        }
    });
